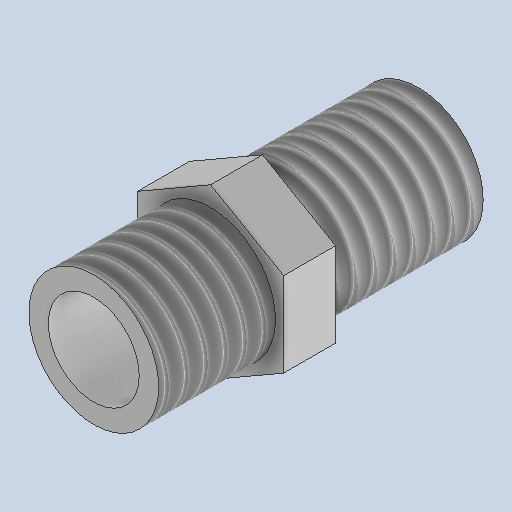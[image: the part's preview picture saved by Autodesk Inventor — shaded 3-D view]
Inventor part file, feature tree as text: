
AUTODESK INVENTOR PART (.ipt)
format: ipt  version: 2025.1 (Build 291241000, 241)  size: 194,560 bytes
history: native  units: mm
features: extrude x4, sketch x4, thread x2
ambient origin geometry x8: Origin, YZ Plane, XZ Plane, XY Plane, X Axis, Y Axis, Z Axis, Center Point
bodies: Volumenkörper1 (feature_tree)
feature tree (10):
  extrude  "Extrusion1"  Depth=13.0mm
  extrude  "Extrusion2"  Depth=12.0mm TaperAngle=0.0deg
  extrude  "Extrusion3"  Depth=12.0mm TaperAngle=0.0deg
  thread  "Gewinde1"  [1 undecoded]
  thread  "Gewinde2"  [1 undecoded]
  extrude  "Extrusion4"  [1 undecoded]
  sketch  "Skizze1"  dims[d0=10.0mm d1=13.0mm]
  sketch  "Skizze2"  dims[d2=4.0mm d3=0.0mm d4=12.0mm d5=0.0mm]
  sketch  "Skizze3"  dims[d6=13.0mm d7=0.0mm d8=12.0mm d9=0.0mm d10=9.0mm d11=0.0mm d12=7.0mm]
  sketch  "Skizze4"  dims[d13=13.0mm d14=0.0mm]
note: 3 required parameter values undecoded (feature->parameter linkage not recoverable at this tier; creation-order binding heuristic only, values carry confidence <= 0.55)
